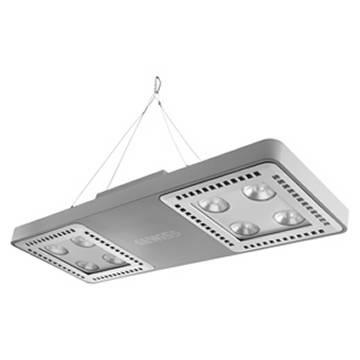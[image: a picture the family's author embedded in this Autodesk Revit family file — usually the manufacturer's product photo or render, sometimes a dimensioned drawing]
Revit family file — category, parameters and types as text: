
# Revit family: Lighting-Industrial-GEWISS-SMART[4]HLO_HIGHBAYS-LED_2M_DALI
name_source: partatom
category: Apparecchi per illuminazione
units: mm (PartAtom-declared; Revit-internal decimal feet)

## family parameters
Basato su piano di lavoro = Sì
Condiviso = No
Numero OmniClass = 23.80.70.00
Punto di calcolo locali = No
Quota connettore circolare = Usa diametro
Sempre verticale = No
Sorgente d'illuminazione = No
Taglio con vuoti quando caricato = No
Tipo di parte = Normale
Titolo OmniClass = Lighting

## types (36) — shared parameters
Application = Internal
Body = PA6 "Halogen Free" loaded fibreglass
Carico apparente = 97 VA
Catalogue = LIGHTING
Classification: = -
Classificazione = Lighting
Color Rendering Index = CRI-80
Colour = Grey RAL 7035
Colour : = Grey RAL 7035
Commenti sul wattaggio = 97W
Context = Lighting for industries and sports facilities
Control System = 1 x DALI DT6
Control System : = DALI
DIN 18032-3 certification = With Bracket - Rope Kit + terminal&nbsp;(in approval)
Device with reduced surface temperature = Yes
Dist_sorg_lum = 10 mm  [stored 0.0328084 ft]
Driver = Included
Driver Box = Built-in
Electrocod = 2444
Eletrical and lighting features = -
External screw = Stainless steel
Fixing = -
Gasket = anti-aging silicone
General information = -
Glow Wire Test : = 850 °C
IDF = f4da8922-e4a4-4281-b810-fd63fbdeb46b
IDT = 39c294b6b8a14fd39c4f066ec01eb55a
IP degree = IP66
IPEA = -
Immagine tipo = GWL1311.jpg
Installationa and maintenance = -
Insulation class = I
LED Maintenance = Non-replaceable
Lampada = LED
Larghezza = 254 mm
Lifetime = L90B10 (Tq+25°C) = 100.000 h - L90B10 (Tq+50°C) = 50.000 h
Locking Hook = -
Luminaire = LED Industrial ReflectorÂ
Lunghezza = 699 mm  [stored 2.29331 ft]
Mascherina = <Per categoria>
Materials = -
Maximum surface exposed to the wind : = 0,184 m²
Motore = <Per categoria>
Mouting and installation = Ceiling - Wallmounting - Suspension
Operating temperature : = -30°C ÷ +50 °C
Optic Maintenance = Non-replaceable
Optic and illuminating features = -
Overvoltage protection = DM 6 kV / CM 10 kV
Photobiological Risk Class = RG0
Produttore = GEWISS S.p.A.
Prospetto di default = 1219 mm
Rated frequency (Hz) = 50/60 Hz
Shield type = Tempered glass Thickness 4mm
Shock resistance = IK08
Spessore plafoniera = 40 mm  [stored 0.131234 ft]
Standard Deviation Colour Matching = SDCM = 3
Standard- = EN 60598-1 ; EN 60598-2-1 ; EN 60598-2-24
Standards and approvals = -
Stocking temperature = -40 +70 °C
Struttura plafoniera = <Per categoria>
Supply voltage = 220 - 240 V
System power = 125W
Technical sheet = https://www.gewiss.com
Tilt- = With bracket accessory
Trasformatore = <Per categoria>
Type of light source = LED - Not replaceable
URL = https://www.gewiss.com
Unique digital code (Datamatrix) = Datamatrix
Version file RFA = 20.11
Voltaggio = 230 V
Warranty = 5 years
Weight (kg): = 6,5
Wiring = With GW connect watertight connector

## per-type parameters (varying)
| type | Colour temperature | Descrizione | Efficiency (lm/W) | Lumen output (lm) | Modello | Optic | Optic : | SEO | Unified Glare Rating |
| GWS4223BH830 - SMART4HB 2M C.PAS.DALI HLO 60° 30K | 3000K | SMART[4]HB 2M C.PAS.DALI HLO 60° 30K | 135 | 16900 | GWS4223BH830 | 60° | Metallic PC reflector and PMMA lenses |  | UGR - 22 |
| GWS4221BP857 - SMART4HB 2M ST.AL.DALI HLO 90° 57K | 5700K | SMART[4]HB 2M ST.AL.DALI HLO 90° 57K | 144 | 18000 | GWS4221BP857 | 90° | Metallic PC reflector and PMMA lenses |  | UGR - 25 |
| GWS4221BA840 - SMART4HB 2M ST.AL.DALI HLO ARR.40K | 4000K | SMART[4]HB 2M ST.AL.DALI HLO ARR.40K | 144 | 18000 | GWS4221BA840 | Array | Metallized polycarbonate reflector |  | - |
| GWS4221BC830 - SMART4HB 2M ST.AL.DALI HLO ASI.30K | 3000K | SMART[4]HB 2M ST.AL.DALI HLO ASI.30K | 122 | 15300 | GWS4221BC830 | Asymmetrical | Metallic PC reflector and PMMA lenses | High bay | - |
| GWS4223BQ830 - SMART4HB 2M C.PAS.DALI HLO ELL.30K | 3000K | SMART[4]HB 2M C.PAS.DALI HLO ELL.30K | 122 | 15300 | GWS4223BQ830 | Elliptical | Metallic PC reflector and PMMA lenses | High bay | - |
| GWS4223BA830 - SMART4HB 2M C.PAS.DALI HLO ARR.30K | 3000K | SMART[4]HB 2M C.PAS.DALI HLO ARR.30K | 138 | 17200 | GWS4223BA830 | Array | Metallized polycarbonate reflector |  | - |
| GWS4221BA830 - SMART4HB 2M ST.AL.DALI HLO ARR.30K | 3000K | SMART[4]HB 2M ST.AL.DALI HLO ARR.30K | 138 | 17200 | GWS4221BA830 | Array | Metallized polycarbonate reflector |  | - |
| GWS4223BH840 - SMART4HB 2M C.PAS.DALI HLO 60° 40K | 4000K | SMART[4]HB 2M C.PAS.DALI HLO 60° 40K | 142 | 17700 | GWS4223BH840 | 60° | Metallic PC reflector and PMMA lenses |  | UGR - 22 |
| GWS4221BC857 - SMART4HB 2M ST.AL.DALI HLO ASI.57K | 5700K | SMART[4]HB 2M ST.AL.DALI HLO ASI.57K | 128 | 16000 | GWS4221BC857 | Asymmetrical | Metallic PC reflector and PMMA lenses | High bay | - |
| GWS4223BA857 - SMART4HB 2M C.PAS.DALI HLO ARR.57K | 5700K | SMART[4]HB 2M C.PAS.DALI HLO ARR.57K | 144 | 18000 | GWS4223BA857 | Array | Metallized polycarbonate reflector |  | - |
| GWS4221BC840 - SMART4HB 2M ST.AL.DALI HLO ASI.40K | 4000K | SMART[4]HB 2M ST.AL.DALI HLO ASI.40K | 128 | 16000 | GWS4221BC840 | Asymmetrical | Metallic PC reflector and PMMA lenses | High bay | - |
| GWS4223BQ840 - SMART4HB 2M C.PAS.DALI HLO ELL.40K | 4000K | SMART[4]HB 2M C.PAS.DALI HLO ELL.40K | 128 | 16000 | GWS4223BQ840 | Elliptical | Metallic PC reflector and PMMA lenses | High bay | - |
| GWS4223BA840 - SMART4HB 2M C.PAS.DALI HLO ARR.40K | 4000K | SMART[4]HB 2M C.PAS.DALI HLO ARR.40K | 144 | 18000 | GWS4223BA840 | Array | Metallized polycarbonate reflector |  | - |
| GWS4223BQ857 - SMART4HB 2M C.PAS.DALI HLO ELL.57K | 5700K | SMART[4]HB 2M C.PAS.DALI HLO ELL.57K | 128 | 16000 | GWS4223BQ857 | Elliptical | Metallic PC reflector and PMMA lenses | High bay | - |
| GWS4221BH840 - SMART4HB 2M ST.AL.DALI HLO 60° 40K | 4000K | SMART[4]HB 2M ST.AL.DALI HLO 60° 40K | 142 | 17700 | GWS4221BH840 | 60° | Metallic PC reflector and PMMA lenses |  | UGR - 22 |
| GWS4221BA857 - SMART4HB 2M ST.AL.DALI HLO ARR.57K | 5700K | SMART[4]HB 2M ST.AL.DALI HLO ARR.57K | 144 | 18000 | GWS4221BA857 | Array | Metallized polycarbonate reflector |  | - |
| GWS4223BF830 - SMART4HB 2M C.PAS.DALI HLO 30° 30K | 3000K | SMART[4]HB 2M C.PAS.DALI HLO 30° 30K | 134 | 16800 | GWS4223BF830 | 30° | Metallic PC reflector and PMMA lenses |  | UGR - 19 |
| GWS4221BQ830 - SMART4HB 2M ST.AL.DALI HLO ELL.30K | 3000K | SMART[4]HB 2M ST.AL.DALI HLO ELL.30K | 122 | 15300 | GWS4221BQ830 | Elliptical | Metallic PC reflector and PMMA lenses | High bay | - |
| GWS4223BF840 - SMART4HB 2M C.PAS.DALI HLO 30° 40K | 4000K | SMART[4]HB 2M C.PAS.DALI HLO 30° 40K | 141 | 17600 | GWS4223BF840 | 30° | Metallic PC reflector and PMMA lenses |  | UGR - 19 |
| GWS4223BP857 - SMART4HB 2M C.PAS.DALI HLO 90° 57K | 5700K | SMART[4]HB 2M C.PAS.DALI HLO 90° 57K | 144 | 18000 | GWS4223BP857 | 90° | Metallic PC reflector and PMMA lenses |  | UGR - 25 |
| GWS4223BH857 - SMART4HB 2M C.PAS.DALI HLO 60° 57K | 5700K | SMART[4]HB 2M C.PAS.DALI HLO 60° 57K | 142 | 17700 | GWS4223BH857 | 60° | Metallic PC reflector and PMMA lenses |  | UGR - 22 |
| GWS4223BP830 - SMART4HB 2M C.PAS.DALI HLO 90° 30K | 3000K | SMART[4]HB 2M C.PAS.DALI HLO 90° 30K | 138 | 17200 | GWS4223BP830 | 90° | Metallic PC reflector and PMMA lenses |  | UGR - 25 |
| GWS4223BC857 - SMART4HB 2M C.PAS.DALI HLO ASI.57K | 5700K | SMART[4]HB 2M C.PAS.DALI HLO ASI.57K | 128 | 16000 | GWS4223BC857 | Asymmetrical | Metallic PC reflector and PMMA lenses | High bay | - |
| GWS4223BP840 - SMART4HB 2M C.PAS.DALI HLO 90° 40K | 4000K | SMART[4]HB 2M C.PAS.DALI HLO 90° 40K | 144 | 18000 | GWS4223BP840 | 90° | Metallic PC reflector and PMMA lenses |  | UGR - 25 |
| GWS4221BF830 - SMART4HB 2M ST.AL.DALI HLO 30° 30K | 3000K | SMART[4]HB 2M ST.AL.DALI HLO 30° 30K | 134 | 16800 | GWS4221BF830 | 30° | Metallic PC reflector and PMMA lenses |  | UGR - 19 |
| GWS4221BF840 - SMART4HB 2M ST.AL.DALI HLO 30° 40K | 4000K | SMART[4]HB 2M ST.AL.DALI HLO 30° 40K | 141 | 17600 | GWS4221BF840 | 30° | Metallic PC reflector and PMMA lenses |  | UGR - 19 |
| GWS4221BF857 - SMART4HB 2M ST.AL.DALI HLO 30° 57K | 5700K | SMART[4]HB 2M ST.AL.DALI HLO 30° 57K | 141 | 17600 | GWS4221BF857 | 30° | Metallic PC reflector and PMMA lenses |  | UGR - 19 |
| GWS4221BQ840 - SMART4HB 2M ST.AL.DALI HLO ELL.40K | 4000K | SMART[4]HB 2M ST.AL.DALI HLO ELL.40K | 128 | 16000 | GWS4221BQ840 | Elliptical | Metallic PC reflector and PMMA lenses | High bay | - |
| GWS4221BP840 - SMART4HB 2M ST.AL.DALI HLO 90° 40K | 4000K | SMART[4]HB 2M ST.AL.DALI HLO 90° 40K | 144 | 18000 | GWS4221BP840 | 90° | Metallic PC reflector and PMMA lenses |  | UGR - 25 |
| GWS4221BH830 - SMART4HB 2M ST.AL.DALI HLO 60° 30K | 3000K | SMART[4]HB 2M ST.AL.DALI HLO 60° 30K | 135 | 16900 | GWS4221BH830 | 60° | Metallic PC reflector and PMMA lenses |  | UGR - 22 |
| GWS4223BC830 - SMART4HB 2M C.PAS.DALI HLO ASI.30K | 3000K | SMART[4]HB 2M C.PAS.DALI HLO ASI.30K | 122 | 15300 | GWS4223BC830 | Asymmetrical | Metallic PC reflector and PMMA lenses | High bay | - |
| GWS4223BF857 - SMART4HB 2M C.PAS.DALI HLO 30° 57K | 5700K | SMART[4]HB 2M C.PAS.DALI HLO 30° 57K | 141 | 17600 | GWS4223BF857 | 30° | Metallic PC reflector and PMMA lenses |  | UGR - 19 |
| GWS4221BQ857 - SMART4HB 2M ST.AL.DALI HLO ELL.57K | 5700K | SMART[4]HB 2M ST.AL.DALI HLO ELL.57K | 128 | 16000 | GWS4221BQ857 | Elliptical | Metallic PC reflector and PMMA lenses | High bay | - |
| GWS4223BC840 - SMART4HB 2M C.PAS.DALI HLO ASI.40K | 4000K | SMART[4]HB 2M C.PAS.DALI HLO ASI.40K | 128 | 16000 | GWS4223BC840 | Asymmetrical | Metallic PC reflector and PMMA lenses | High bay | - |
| GWS4221BP830 - SMART4HB 2M ST.AL.DALI HLO 90° 30K | 3000K | SMART[4]HB 2M ST.AL.DALI HLO 90° 30K | 138 | 17200 | GWS4221BP830 | 90° | Metallic PC reflector and PMMA lenses |  | UGR - 25 |
| GWS4221BH857 - SMART4HB 2M ST.AL.DALI HLO 60° 57K | 5700K | SMART[4]HB 2M ST.AL.DALI HLO 60° 57K | 142 | 17700 | GWS4221BH857 | 60° | Metallic PC reflector and PMMA lenses |  | UGR - 22 |

note: [stored X ft] marks values corroborated as IEEE doubles in the binary element streams (Revit-internal decimal feet)

## geometry (parser evidence)
native form markers: Blend x4, Sweep x3
no freeform markers — native parametric forms only
